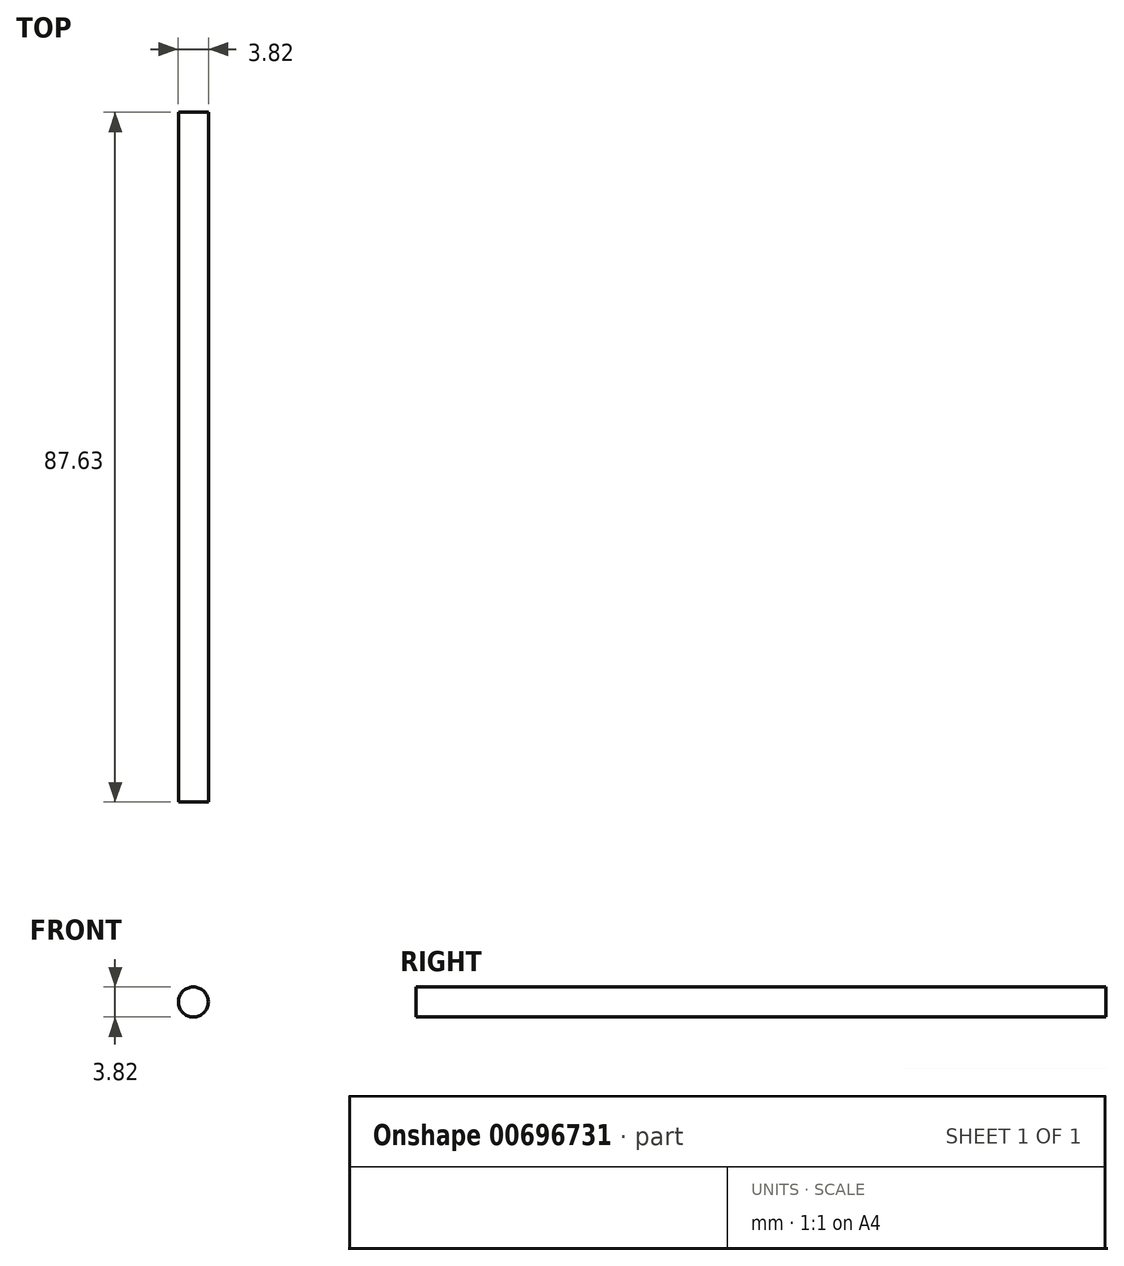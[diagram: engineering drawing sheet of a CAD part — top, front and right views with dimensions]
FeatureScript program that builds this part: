
annotation { "Feature Type Name" : "Feature", "Feature Type Description" : "" }
export const myFeature = defineFeature(function(context is Context, id is Id, definition is map)
    precondition{}
    {
        {
            var Q0;
            Q0=qCreatedBy(makeId("Front.planeOp"),FACE);
            var sketch = newSketch(context, id + "F0", { "sketchPlane" : qUnion([Q0])});
            skCircle(sketch, "E0", {"center": v(0, 0) * mm, "radius": 1.9 * mm});
            skSolve(sketch);
        }
        {
            var Q0;
            Q0=makeQuery(id+"F0.imprint","IMPRINT",FACE,{"disambiguationData":[TD([[makeQuery(id+"F0.imprint","IMPRINT",EDGE,{"derivedFrom":sQuery(id+"F0.wireOp",EDGE,"E0")}),1.0]])]});
            extrude(context, id + "F1", {"entities" : qUnion([Q0]), "depth" : 87.63 * mm, "offsetDistance" : 25.4 * mm});
        }
    });
